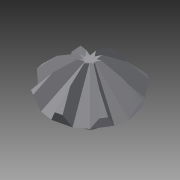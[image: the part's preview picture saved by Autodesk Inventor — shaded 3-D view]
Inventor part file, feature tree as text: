
AUTODESK INVENTOR PART (.ipt)
format: ipt  version: 2015 (Build 190159000, 159)  size: 142,336 bytes
history: native  units: in
note: dims shown in document units (in); Inventor stores cm internally (conversion verified against a paired STEP export)
features: extrude x3, sketch x3, pattern_circular x2, chamfer x1
ambient origin geometry x8: Origin, YZ Plane, XZ Plane, XY Plane, X Axis, Y Axis, Z Axis, Center Point
bodies: Body1 (feature_tree)
feature tree (9):
  extrude  "Extrusion6"  TaperAngle=45.0deg  [1 undecoded]
  chamfer  "Chamfer2"  Distance=0.75in
  pattern_circular  "Circular Pattern3"  Count=8 Angle=360.0deg
  extrude  "Extrusion7"  Depth=0.5in
  extrude  "Extrusion8"  Depth=0.5in TaperAngle=0.0deg
  pattern_circular  "Circular Pattern4"  Count=8 Angle=360.0deg
  sketch  "Sketch7"  dims[d25=0.875in d26=45.0deg d27=0.75in d28=0.0in]
  sketch  "Sketch8"  dims[d29=0.75in d30=0.125in d31=45.0deg d32=3.1496in d33=360.0deg]
  sketch  "Sketch9"  dims[d35=0.25in d36=-0.1622in d37=0.375in d38=0.5in d39=0.0in d40=3.1496in d41=360.0deg]
note: 1 required parameter value undecoded (feature->parameter linkage not recoverable at this tier; creation-order binding heuristic only, values carry confidence <= 0.55)
